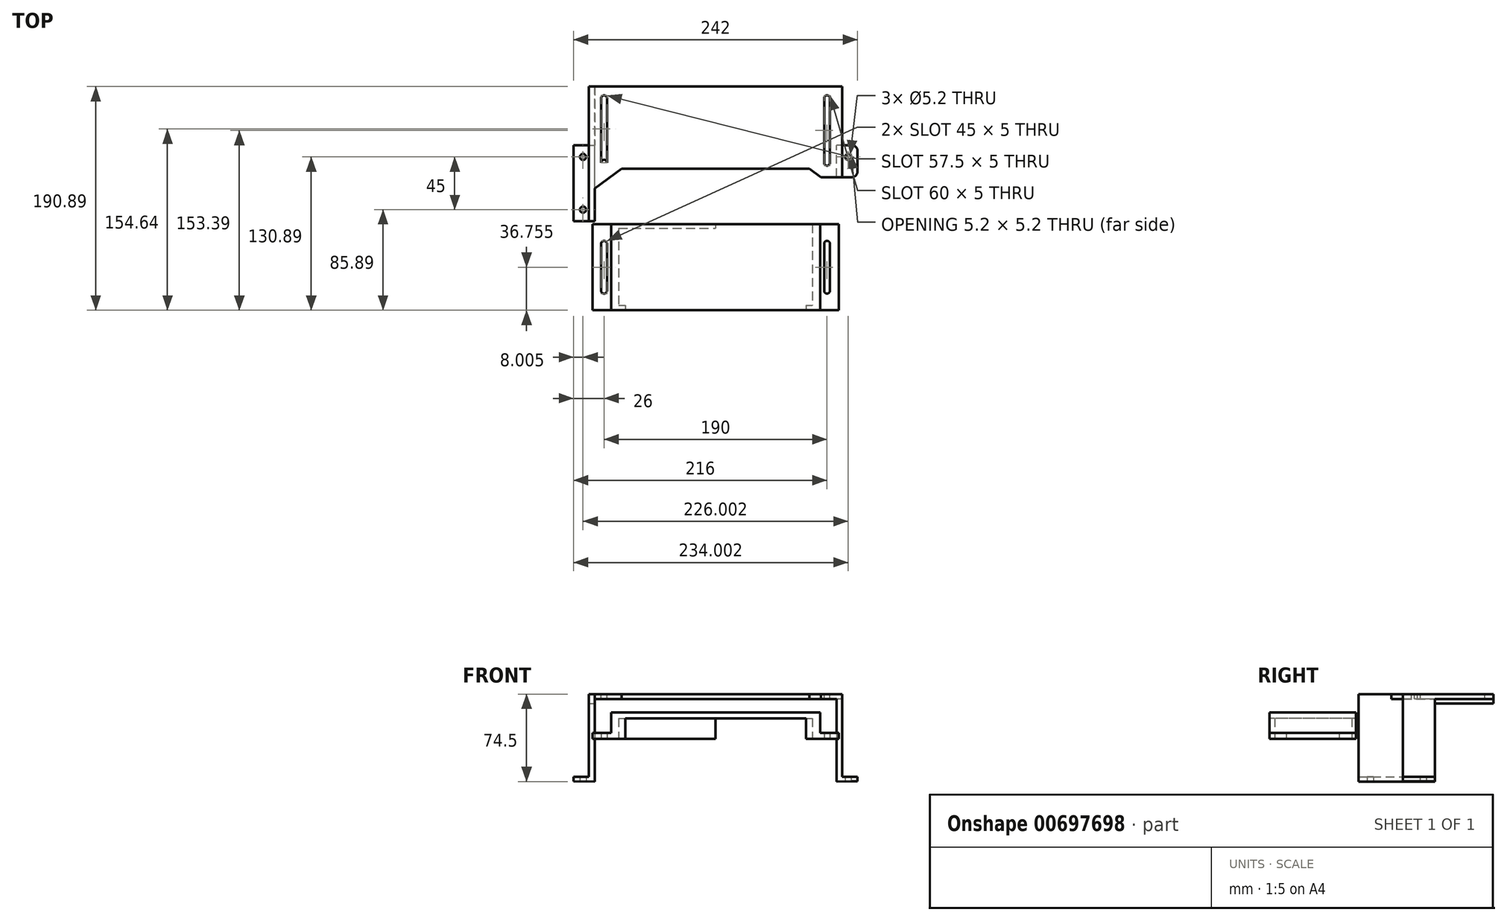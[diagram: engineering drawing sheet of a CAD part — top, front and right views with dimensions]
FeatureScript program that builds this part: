
annotation { "Feature Type Name" : "Feature", "Feature Type Description" : "" }
export const myFeature = defineFeature(function(context is Context, id is Id, definition is map)
    precondition{}
    {
        {
            var Q0;
            Q0=qCreatedBy(makeId("Front.planeOp"),FACE);
            var sketch = newSketch(context, id + "F0", { "sketchPlane" : qUnion([Q0])});
            skLineSegment(sketch, "E0.top", {"start": v(108, 38) * mm, "end": v(-108, 38) * mm});
            skPoint(sketch, "E0.middle", {"position": v(0, 0) * mm});
            skLineSegment(sketch, "E1.top", {"start": v(103, 34) * mm, "end": v(-103, 34) * mm});
            skLineSegment(sketch, "E2.MirrorCS", {"start": v(121, -32.45) * mm, "end": v(108, -32.5) * mm});
            skLineSegment(sketch, "E3.MirrorCS", {"start": v(121, -36.45) * mm, "end": v(121, -32.45) * mm});
            skLineSegment(sketch, "E4", {"start": v(108, 38) * mm, "end": v(108, -32.5) * mm});
            skLineSegment(sketch, "E5", {"start": v(121, -36.45) * mm, "end": v(103, -36.5) * mm});
            skLineSegment(sketch, "E6", {"start": v(103, 34) * mm, "end": v(103, -36.5) * mm});
            skLineSegment(sketch, "E7.MirrorCS", {"start": v(-103, 34) * mm, "end": v(-103, -36.5) * mm});
            skLineSegment(sketch, "E8.MirrorCS", {"start": v(-108, 38) * mm, "end": v(-108, -32.5) * mm});
            skLineSegment(sketch, "E9.MirrorCS", {"start": v(-121, -36.45) * mm, "end": v(-103, -36.5) * mm});
            skLineSegment(sketch, "E10.MirrorCS", {"start": v(-121, -36.45) * mm, "end": v(-121, -32.45) * mm});
            skLineSegment(sketch, "E11.MirrorCS", {"start": v(-121, -32.45) * mm, "end": v(-108, -32.5) * mm});
            skLineSegment(sketch, "E12", {"start": v(0, 34) * mm, "end": v(0, 0) * mm});
            skSolve(sketch);
        }
        {
            var Q0;
            Q0=makeQuery(id+"F0.imprint","IMPRINT",FACE,{"disambiguationData":[TD([[makeQuery(id+"F0.imprint","IMPRINT",EDGE,{"derivedFrom":sQuery(id+"F0.wireOp",EDGE,"E0.top")}),1.0]])]});
            extrude(context, id + "F1", {"entities" : qUnion([Q0]), "depth" : 65 * mm, "offsetDistance" : 25 * mm});
        }
        {
            var Q0;
            Q0=makeQuery(id+"F1.opExtrude","SWEPT_FACE",FACE,{"disambiguationData":[OSD([sQuery(id+"F0.wireOp",EDGE,"E0.top")])]});
            var sketch = newSketch(context, id + "F2", { "sketchPlane" : qUnion([Q0])});
            skLineSegment(sketch, "E13.bottom", {"start": v(80, -65) * mm, "end": v(-80, -65) * mm});
            skLineSegment(sketch, "E13.top", {"start": v(80, -20) * mm, "end": v(-80, -20) * mm});
            skLineSegment(sketch, "E13.left", {"start": v(80, -65) * mm, "end": v(80, -20) * mm});
            skLineSegment(sketch, "E13.right", {"start": v(-80, -65) * mm, "end": v(-80, -20) * mm});
            skPoint(sketch, "E13.middle", {"position": v(0, -42.5) * mm});
            skLineSegment(sketch, "E14.MirrorCS", {"start": v(80, -20) * mm, "end": v(107, -40) * mm});
            skLineSegment(sketch, "E15", {"start": v(107, -40) * mm, "end": v(107, -65) * mm});
            skLineSegment(sketch, "E16.MirrorCS", {"start": v(-80, -20) * mm, "end": v(-107, -40) * mm});
            skLineSegment(sketch, "E17.MirrorCS", {"start": v(-107, -40) * mm, "end": v(-107, -65) * mm});
            skLineSegment(sketch, "E18", {"start": v(108, -65) * mm, "end": v(112, -65) * mm});
            skLineSegment(sketch, "E19", {"start": v(112, -65) * mm, "end": v(112, 122.22) * mm});
            skLineSegment(sketch, "E20.MirrorCS", {"start": v(-112, -65) * mm, "end": v(-112, 122.22) * mm});
            skLineSegment(sketch, "E21", {"start": v(-103, -37.04) * mm, "end": v(-103, -65) * mm});
            skSolve(sketch);
        }
        {
            var Q0;
            Q0=makeQuery(id+"F2.imprint","IMPRINT",FACE,{"disambiguationData":[TD([[makeQuery(id+"F2.imprint","IMPRINT",EDGE,{"derivedFrom":sQuery(id+"F2.wireOp",EDGE,"E13.bottom")}),-1.0]])]});
            var Q1;
            {var subQ0=sQuery(id+"F2.wireOp",EDGE,"E13.left");Q1=makeQuery(id+"F2.imprint","IMPRINT",FACE,{"disambiguationData":[TD([[makeQuery(id+"F2.imprint","IMPRINT",EDGE,{"derivedFrom":subQ0}),-1.0]])]});}
            var Q2;
            {var subQ0=sQuery(id+"F2.wireOp",EDGE,"E13.right");Q2=makeQuery(id+"F2.imprint","IMPRINT",FACE,{"disambiguationData":[TD([[makeQuery(id+"F2.imprint","IMPRINT",EDGE,{"derivedFrom":subQ0}),1.0]])]});}
            var Q3;
            Q3=makeQuery(id+"F1.opExtrude","SWEPT_FACE",FACE,{"disambiguationData":[OSD([sQuery(id+"F0.wireOp",EDGE,"E1.top")])]});
            extrude(context, id + "F3", {"entities" : qUnion([Q0, Q1, Q2]), "operationType" : NewBodyOperationType.REMOVE, "endBound" : BoundingType.UP_TO_SURFACE, "oppositeDirection" : true, "depth" : 25 * mm, "endBoundEntityFace" : qUnion([Q3]), "offsetDistance" : 25 * mm});
        }
        {
            var Q0;
            Q0=makeQuery(id+"F1.opExtrude","CAP_FACE",FACE,{"disambiguationData":[OSD([sQuery(id+"F0.wireOp",EDGE,"E0.bottom"),sQuery(id+"F0.wireOp",EDGE,"E0.top"),sQuery(id+"F0.wireOp",EDGE,"E0.left"),sQuery(id+"F0.wireOp",EDGE,"E0.right"),sQuery(id+"F0.wireOp",EDGE,"E1.top"),sQuery(id+"F0.wireOp",EDGE,"E1.left"),sQuery(id+"F0.wireOp",EDGE,"E1.right"),sQuery(id+"F0.wireOp",EDGE,"vjw2G5nG-7NAh-i6nb-pNf6-F4kYSanWr40I.bottom"),sQuery(id+"F0.wireOp",EDGE,"vjw2G5nG-7NAh-i6nb-pNf6-F4kYSanWr40I.top"),sQuery(id+"F0.wireOp",EDGE,"vjw2G5nG-7NAh-i6nb-pNf6-F4kYSanWr40I.right"),sQuery(id+"F0.wireOp",EDGE,"50cf3a80-4362-4fa1-9d3c-48074abaa2c80.MirrorCS"),sQuery(id+"F0.wireOp",EDGE,"50cf3a80-4362-4fa1-9d3c-48074abaa2c81.MirrorCS"),sQuery(id+"F0.wireOp",EDGE,"50cf3a80-4362-4fa1-9d3c-48074abaa2c82.MirrorCS"),sQuery(id+"F0.wireOp",EDGE,"gSBNCoDe-7ixm-a6xe-L2ER-ax2OvEirnCgN"),sQuery(id+"F0.wireOp",EDGE,"e99ea971-1385-4194-99fd-02c7cae5d03b0.MirrorCS"),sQuery(id+"F0.wireOp",EDGE,"f15c71dd-c8da-4e97-9559-117df91addcc.trimOffspring")])],"isStart":true});
            var sketch = newSketch(context, id + "F4", { "sketchPlane" : qUnion([Q0])});
            skLineSegment(sketch, "E22.bottom", {"start": v(-108, 38) * mm, "end": v(103, 38) * mm});
            skLineSegment(sketch, "E22.top", {"start": v(-108, 34) * mm, "end": v(103, 34) * mm});
            skLineSegment(sketch, "E22.left", {"start": v(-108, 38) * mm, "end": v(-108, 34) * mm});
            skLineSegment(sketch, "E22.right", {"start": v(103, 38) * mm, "end": v(103, 34) * mm});
            skLineSegment(sketch, "E23.bottom", {"start": v(-108, 34) * mm, "end": v(-103, 34) * mm});
            skLineSegment(sketch, "E23.top", {"start": v(-108, 30) * mm, "end": v(-103, 30) * mm});
            skLineSegment(sketch, "E23.left", {"start": v(-108, 34) * mm, "end": v(-108, 30) * mm});
            skLineSegment(sketch, "E23.right", {"start": v(-103, 34) * mm, "end": v(-103, 30) * mm});
            skLineSegment(sketch, "E24.MirrorCS", {"start": v(108, 30) * mm, "end": v(103, 30) * mm});
            skLineSegment(sketch, "E25.MirrorCS", {"start": v(108, 34) * mm, "end": v(108, 30) * mm});
            skLineSegment(sketch, "E26.MirrorCS", {"start": v(103, 34) * mm, "end": v(103, 30) * mm});
            skSolve(sketch);
        }
        {
            var Q0;
            Q0=makeQuery(id+"F4.imprint","IMPRINT",FACE,{"disambiguationData":[TD([[makeQuery(id+"F4.imprint","IMPRINT",EDGE,{"derivedFrom":sQuery(id+"F4.wireOp",EDGE,"E22.bottom")}),-1.0]])]});
            var Q1;
            Q1=makeQuery(id+"F4.imprint","IMPRINT",FACE,{"disambiguationData":[TD([[makeQuery(id+"F4.imprint","IMPRINT",EDGE,{"derivedFrom":sQuery(id+"F4.wireOp",EDGE,"E23.bottom")}),-1.0]])]});
            var Q2;
            Q2=makeQuery(id+"F4.imprint","IMPRINT",FACE,{"disambiguationData":[TD([[makeQuery(id+"F4.imprint","IMPRINT",EDGE,{"derivedFrom":sQuery(id+"F4.wireOp",EDGE,"E24.MirrorCS")}),-1.0]])]});
            extrude(context, id + "F5", {"entities" : qUnion([Q0, Q1, Q2]), "operationType" : NewBodyOperationType.ADD, "depth" : 50 * mm, "offsetDistance" : 25 * mm});
        }
        {
            var Q0;
            Q0=makeQuery(id+"F5.boolean.opBoolean","MERGE",FACE,{"derivedFrom":[makeQuery(id+"F1.opExtrude","SWEPT_FACE",FACE,{"disambiguationData":[OSD([sQuery(id+"F0.wireOp",EDGE,"E0.left")])]}),makeQuery(id+"F5.opExtrude","SWEPT_FACE",FACE,{"disambiguationData":[OSD([sQuery(id+"F4.wireOp",EDGE,"E22.left"),sQuery(id+"F4.wireOp",EDGE,"E23.left")])]})]});
            var sketch = newSketch(context, id + "F6", { "sketchPlane" : qUnion([Q0])});
            skLineSegment(sketch, "E27.bottom", {"start": v(-27.27, 38) * mm, "end": v(-65, 38) * mm});
            skLineSegment(sketch, "E27.top", {"start": v(-27.27, -37.37) * mm, "end": v(-65, -37.37) * mm});
            skLineSegment(sketch, "E27.left", {"start": v(-27.27, 38) * mm, "end": v(-27.27, -37.37) * mm});
            skLineSegment(sketch, "E27.right", {"start": v(-65, 38) * mm, "end": v(-65, -37.37) * mm});
            skSolve(sketch);
        }
        {
            var Q0;
            {var subQ0=sQuery(id+"F6.wireOp",EDGE,"E27.bottom");Q0=makeQuery(id+"F6.imprint","IMPRINT",FACE,{"disambiguationData":[TD([[makeQuery(id+"F6.imprint","IMPRINT",EDGE,{"derivedFrom":subQ0}),-1.0]])]});}
            var Q1;
            {var subQ0=sQuery(id+"F6.wireOp",EDGE,"E27.top");Q1=makeQuery(id+"F6.imprint","IMPRINT",FACE,{"disambiguationData":[TD([[makeQuery(id+"F6.imprint","IMPRINT",EDGE,{"derivedFrom":subQ0}),-1.0]])]});}
            extrude(context, id + "F7", {"entities" : qUnion([Q0, Q1]), "operationType" : NewBodyOperationType.REMOVE, "oppositeDirection" : true, "depth" : 50 * mm, "offsetDistance" : 25 * mm, "symmetric" : true});
        }
        {
            var Q0;
            Q0=makeQuery(id+"F1.opExtrude","SWEPT_FACE",FACE,{"disambiguationData":[OSD([sQuery(id+"F0.wireOp",EDGE,"E9.MirrorCS")])]});
            var sketch = newSketch(context, id + "F8", { "sketchPlane" : qUnion([Q0])});
            skCircle(sketch, "E28", {"center": v(-112.9, 10) * mm, "radius": 2.6 * mm});
            skLineSegment(sketch, "E29", {"start": v(-112.9, 10) * mm, "end": v(-112.9, 55) * mm});
            skCircle(sketch, "E30", {"center": v(-112.9, 55) * mm, "radius": 2.6 * mm});
            skCircle(sketch, "E31.MirrorC", {"center": v(113.1, 55) * mm, "radius": 2.6 * mm});
            skCircle(sketch, "E32.MirrorC", {"center": v(113.1, 10) * mm, "radius": 2.6 * mm});
            skSolve(sketch);
        }
        {
            var Q0;
            Q0 = qSketchRegion(id + "F8", true);
            extrude(context, id + "F9", {"entities" : qUnion([Q0]), "operationType" : NewBodyOperationType.REMOVE, "oppositeDirection" : true, "depth" : 25 * mm, "offsetDistance" : 25 * mm});
        }
        {
            var Q0;
            Q0=makeQuery(id+"F1.opExtrude","CAP_EDGE",EDGE,{"disambiguationData":[OSD([sQuery(id+"F0.wireOp",EDGE,"vjw2G5nG-7NAh-i6nb-pNf6-F4kYSanWr40I.right")])],"isStart":false});
            var Q1;
            Q1=makeQuery(id+"F1.opExtrude","CAP_EDGE",EDGE,{"disambiguationData":[OSD([sQuery(id+"F0.wireOp",EDGE,"50cf3a80-4362-4fa1-9d3c-48074abaa2c80.MirrorCS"),sQuery(id+"F0.wireOp",EDGE,"E3.MirrorCS")])],"isStart":true});
            var Q2;
            Q2=makeQuery(id+"F7.boolean.opBoolean","INTERSECT",EDGE,{"derivedFrom":[makeQuery(id+"F1.opExtrude","SWEPT_FACE",FACE,{"disambiguationData":[OSD([sQuery(id+"F0.wireOp",EDGE,"50cf3a80-4362-4fa1-9d3c-48074abaa2c80.MirrorCS"),sQuery(id+"F0.wireOp",EDGE,"E3.MirrorCS")])]}),makeQuery(id+"F7.opExtrude","SWEPT_FACE",FACE,{"disambiguationData":[OSD([sQuery(id+"F6.wireOp",EDGE,"E27.left")])]})]});
            fillet(context, id + "F10", {"entities" : qUnion([Q0, Q1, Q2]), "radius" : 5 * mm, "tangentPropagation" : true, "allowEdgeOverflow" : false});
        }
        {
            var Q0;
            Q0=makeQuery(id+"F5.boolean.opBoolean","MERGE",FACE,{"derivedFrom":[makeQuery(id+"F1.opExtrude","SWEPT_FACE",FACE,{"disambiguationData":[OSD([sQuery(id+"F0.wireOp",EDGE,"E0.top")])]}),makeQuery(id+"F5.opExtrude","SWEPT_FACE",FACE,{"disambiguationData":[OSD([sQuery(id+"F4.wireOp",EDGE,"E22.bottom")])]})]});
            var sketch = newSketch(context, id + "F11", { "sketchPlane" : qUnion([Q0])});
            skLineSegment(sketch, "E33.bottom", {"start": v(-95, 0) * mm, "end": v(95, 0) * mm});
            skLineSegment(sketch, "E33.top", {"start": v(-95, 40) * mm, "end": v(95, 40) * mm});
            skLineSegment(sketch, "E33.left", {"start": v(-95, 0) * mm, "end": v(-95, 40) * mm});
            skLineSegment(sketch, "E33.right", {"start": v(95, 0) * mm, "end": v(95, 40) * mm});
            skPoint(sketch, "E33.middle", {"position": v(0, 20) * mm});
            skCircle(sketch, "E34", {"center": v(-95, 40) * mm, "radius": 2.5 * mm});
            skLineSegment(sketch, "E35.bottom", {"start": v(82.5, -12.75) * mm, "end": v(-82.5, -12.75) * mm});
            skLineSegment(sketch, "E35.top", {"start": v(82.5, 52.75) * mm, "end": v(-82.5, 52.75) * mm});
            skLineSegment(sketch, "E35.left", {"start": v(82.5, -12.75) * mm, "end": v(82.5, 52.75) * mm});
            skLineSegment(sketch, "E35.right", {"start": v(-82.5, -12.75) * mm, "end": v(-82.5, 52.75) * mm});
            skLineSegment(sketch, "E36", {"start": v(0, 20) * mm, "end": v(12, 20) * mm});
            skCircle(sketch, "E37.MirrorC", {"center": v(-95, 0) * mm, "radius": 2.5 * mm});
            skCircle(sketch, "E38.MirrorC", {"center": v(95, 40) * mm, "radius": 2.5 * mm});
            skCircle(sketch, "E39.MirrorC", {"center": v(95, 0) * mm, "radius": 2.5 * mm});
            skLineSegment(sketch, "E40", {"start": v(95, 0) * mm, "end": v(95, -15) * mm});
            skCircle(sketch, "E41", {"center": v(95, -15) * mm, "radius": 2.5 * mm});
            skLineSegment(sketch, "E42", {"start": v(97.5, -15) * mm, "end": v(97.5, 40) * mm});
            skLineSegment(sketch, "E43", {"start": v(92.5, -15) * mm, "end": v(92.5, 40) * mm});
            skLineSegment(sketch, "E44.MirrorCS", {"start": v(-92.5, -15) * mm, "end": v(-92.5, 40) * mm});
            skLineSegment(sketch, "E45.MirrorCS", {"start": v(-97.5, -15) * mm, "end": v(-97.5, 40) * mm});
            skCircle(sketch, "E46.MirrorC", {"center": v(-95, -15) * mm, "radius": 2.5 * mm});
            skSolve(sketch);
        }
        {
            var Q0;
            {var subQ0=sQuery(id+"F11.wireOp",EDGE,"E33.left");var subQ1=sQuery(id+"F11.wireOp",EDGE,"E33.top");var subQ2=makeQuery(id+"F11.imprint","INTERSECT",VERTEX,{"derivedFrom":[subQ1,subQ0]});Q0=makeQuery(id+"F11.imprint","IMPRINT",FACE,{"disambiguationData":[TD([[makeQuery(id+"F11.imprint","IMPRINT",EDGE,{"disambiguationData":[TD([[subQ2,-1.0]])],"derivedFrom":subQ1}),1.0]])]});}
            var Q1;
            {var subQ0=sQuery(id+"F11.wireOp",EDGE,"E33.left");var subQ1=sQuery(id+"F11.wireOp",EDGE,"E33.top");var subQ2=makeQuery(id+"F11.imprint","INTERSECT",VERTEX,{"derivedFrom":[subQ1,subQ0]});Q1=makeQuery(id+"F11.imprint","IMPRINT",FACE,{"disambiguationData":[TD([[makeQuery(id+"F11.imprint","IMPRINT",EDGE,{"disambiguationData":[TD([[subQ2,-1.0]])],"derivedFrom":subQ1}),-1.0]])]});}
            var Q2;
            {var subQ0=sQuery(id+"F11.wireOp",EDGE,"E33.left");var subQ1=sQuery(id+"F11.wireOp",EDGE,"E33.bottom");var subQ2=makeQuery(id+"F11.imprint","INTERSECT",VERTEX,{"derivedFrom":[subQ1,subQ0]});Q2=makeQuery(id+"F11.imprint","IMPRINT",FACE,{"disambiguationData":[TD([[makeQuery(id+"F11.imprint","IMPRINT",EDGE,{"disambiguationData":[TD([[subQ2,-1.0]])],"derivedFrom":subQ1}),-1.0]])]});}
            var Q3;
            {var subQ0=sQuery(id+"F11.wireOp",EDGE,"E33.left");var subQ1=sQuery(id+"F11.wireOp",EDGE,"E33.bottom");var subQ2=makeQuery(id+"F11.imprint","INTERSECT",VERTEX,{"derivedFrom":[subQ1,subQ0]});Q3=makeQuery(id+"F11.imprint","IMPRINT",FACE,{"disambiguationData":[TD([[makeQuery(id+"F11.imprint","IMPRINT",EDGE,{"disambiguationData":[TD([[subQ2,-1.0]])],"derivedFrom":subQ1}),1.0]])]});}
            var Q4;
            {var subQ0=sQuery(id+"F11.wireOp",EDGE,"E33.right");var subQ1=sQuery(id+"F11.wireOp",EDGE,"E33.bottom");var subQ2=makeQuery(id+"F11.imprint","INTERSECT",VERTEX,{"derivedFrom":[subQ1,subQ0]});Q4=makeQuery(id+"F11.imprint","IMPRINT",FACE,{"disambiguationData":[TD([[makeQuery(id+"F11.imprint","IMPRINT",EDGE,{"disambiguationData":[TD([[subQ2,1.0]])],"derivedFrom":subQ1}),-1.0]])]});}
            var Q5;
            {var subQ0=sQuery(id+"F11.wireOp",EDGE,"E33.right");var subQ1=sQuery(id+"F11.wireOp",EDGE,"E33.bottom");var subQ2=makeQuery(id+"F11.imprint","INTERSECT",VERTEX,{"derivedFrom":[subQ1,subQ0]});Q5=makeQuery(id+"F11.imprint","IMPRINT",FACE,{"disambiguationData":[TD([[makeQuery(id+"F11.imprint","IMPRINT",EDGE,{"disambiguationData":[TD([[subQ2,1.0]])],"derivedFrom":subQ1}),1.0]])]});}
            var Q6;
            {var subQ0=sQuery(id+"F11.wireOp",EDGE,"E33.right");var subQ1=sQuery(id+"F11.wireOp",EDGE,"E33.top");var subQ2=makeQuery(id+"F11.imprint","INTERSECT",VERTEX,{"derivedFrom":[subQ1,subQ0]});Q6=makeQuery(id+"F11.imprint","IMPRINT",FACE,{"disambiguationData":[TD([[makeQuery(id+"F11.imprint","IMPRINT",EDGE,{"disambiguationData":[TD([[subQ2,1.0]])],"derivedFrom":subQ1}),1.0]])]});}
            var Q7;
            {var subQ0=sQuery(id+"F11.wireOp",EDGE,"E33.right");var subQ1=sQuery(id+"F11.wireOp",EDGE,"E33.top");var subQ2=makeQuery(id+"F11.imprint","INTERSECT",VERTEX,{"derivedFrom":[subQ1,subQ0]});Q7=makeQuery(id+"F11.imprint","IMPRINT",FACE,{"disambiguationData":[TD([[makeQuery(id+"F11.imprint","IMPRINT",EDGE,{"disambiguationData":[TD([[subQ2,1.0]])],"derivedFrom":subQ1}),-1.0]])]});}
            var Q8;
            {var subQ0=sQuery(id+"F11.wireOp",EDGE,"E39.MirrorC");var subQ1=sQuery(id+"F11.wireOp",EDGE,"E33.right");var subQ2=makeQuery(id+"F11.imprint","INTERSECT",VERTEX,{"derivedFrom":[subQ1,subQ0]});Q8=makeQuery(id+"F11.imprint","IMPRINT",FACE,{"disambiguationData":[TD([[makeQuery(id+"F11.imprint","IMPRINT",EDGE,{"disambiguationData":[TD([[subQ2,-1.0]])],"derivedFrom":subQ1}),-1.0]])]});}
            var Q9;
            {var subQ0=sQuery(id+"F11.wireOp",EDGE,"E40");var subQ3=sQuery(id+"F11.wireOp",EDGE,"E39.MirrorC");var subQ5=makeQuery(id+"F11.imprint","INTERSECT",VERTEX,{"derivedFrom":[subQ3,subQ0]});Q9=makeQuery(id+"F11.imprint","IMPRINT",FACE,{"disambiguationData":[TD([[makeQuery(id+"F11.imprint","IMPRINT",EDGE,{"disambiguationData":[TD([[subQ5,-1.0]])],"derivedFrom":subQ3}),1.0]])]});}
            var Q10;
            {var subQ0=sQuery(id+"F11.wireOp",EDGE,"E40");var subQ1=sQuery(id+"F11.wireOp",EDGE,"E39.MirrorC");var subQ2=makeQuery(id+"F11.imprint","INTERSECT",VERTEX,{"derivedFrom":[subQ1,subQ0]});Q10=makeQuery(id+"F11.imprint","IMPRINT",FACE,{"disambiguationData":[TD([[makeQuery(id+"F11.imprint","IMPRINT",EDGE,{"disambiguationData":[TD([[subQ2,-1.0]])],"derivedFrom":subQ1}),-1.0]])]});}
            var Q11;
            {var subQ0=sQuery(id+"F11.wireOp",EDGE,"E41");var subQ1=makeQuery(id+"F11.imprint","INTERSECT",VERTEX,{"derivedFrom":[subQ0,sQuery(id+"F11.wireOp",EDGE,"E42")]});Q11=makeQuery(id+"F11.imprint","IMPRINT",FACE,{"disambiguationData":[TD([[makeQuery(id+"F11.imprint","IMPRINT",EDGE,{"disambiguationData":[TD([[subQ1,-1.0]])],"derivedFrom":subQ0}),1.0]])]});}
            var Q12;
            {var subQ0=sQuery(id+"F11.wireOp",EDGE,"E39.MirrorC");var subQ1=sQuery(id+"F11.wireOp",EDGE,"E33.right");var subQ2=makeQuery(id+"F11.imprint","INTERSECT",VERTEX,{"derivedFrom":[subQ1,subQ0]});Q12=makeQuery(id+"F11.imprint","IMPRINT",FACE,{"disambiguationData":[TD([[makeQuery(id+"F11.imprint","IMPRINT",EDGE,{"disambiguationData":[TD([[subQ2,-1.0]])],"derivedFrom":subQ1}),1.0]])]});}
            var Q13;
            {var subQ0=sQuery(id+"F11.wireOp",EDGE,"E40");var subQ5=sQuery(id+"F11.wireOp",EDGE,"E41");var subQ6=makeQuery(id+"F11.imprint","INTERSECT",VERTEX,{"derivedFrom":[subQ0,subQ5]});Q13=makeQuery(id+"F11.imprint","IMPRINT",FACE,{"disambiguationData":[TD([[makeQuery(id+"F11.imprint","IMPRINT",EDGE,{"disambiguationData":[TD([[subQ6,1.0]])],"derivedFrom":subQ0}),-1.0]])]});}
            var Q14;
            {var subQ0=sQuery(id+"F11.wireOp",EDGE,"E37.MirrorC");var subQ1=sQuery(id+"F11.wireOp",EDGE,"E33.left");var subQ2=makeQuery(id+"F11.imprint","INTERSECT",VERTEX,{"derivedFrom":[subQ1,subQ0]});Q14=makeQuery(id+"F11.imprint","IMPRINT",FACE,{"disambiguationData":[TD([[makeQuery(id+"F11.imprint","IMPRINT",EDGE,{"disambiguationData":[TD([[subQ2,-1.0]])],"derivedFrom":subQ1}),-1.0]])]});}
            var Q15;
            {var subQ0=sQuery(id+"F11.wireOp",EDGE,"E37.MirrorC");var subQ1=sQuery(id+"F11.wireOp",EDGE,"E33.left");var subQ2=makeQuery(id+"F11.imprint","INTERSECT",VERTEX,{"derivedFrom":[subQ1,subQ0]});Q15=makeQuery(id+"F11.imprint","IMPRINT",FACE,{"disambiguationData":[TD([[makeQuery(id+"F11.imprint","IMPRINT",EDGE,{"disambiguationData":[TD([[subQ2,-1.0]])],"derivedFrom":subQ1}),1.0]])]});}
            var Q16;
            {var subQ0=sQuery(id+"F11.wireOp",EDGE,"E46.MirrorC");var subQ1=makeQuery(id+"F11.imprint","INTERSECT",VERTEX,{"derivedFrom":[sQuery(id+"F11.wireOp",EDGE,"E44.MirrorCS"),subQ0]});Q16=makeQuery(id+"F11.imprint","IMPRINT",FACE,{"disambiguationData":[TD([[makeQuery(id+"F11.imprint","IMPRINT",EDGE,{"disambiguationData":[TD([[subQ1,1.0]])],"derivedFrom":subQ0}),-1.0]])]});}
            var Q17;
            {var subQ0=sQuery(id+"F11.wireOp",EDGE,"E45.MirrorCS");var subQ5=sQuery(id+"F11.wireOp",EDGE,"E46.MirrorC");var subQ7=makeQuery(id+"F11.imprint","INTERSECT",VERTEX,{"derivedFrom":[subQ0,subQ5]});Q17=makeQuery(id+"F11.imprint","IMPRINT",FACE,{"disambiguationData":[TD([[makeQuery(id+"F11.imprint","IMPRINT",EDGE,{"disambiguationData":[TD([[subQ7,-1.0]])],"derivedFrom":subQ0}),-1.0]])]});}
            extrude(context, id + "F12", {"entities" : qUnion([Q0, Q1, Q2, Q3, Q4, Q5, Q6, Q7, Q8, Q9, Q10, Q11, Q12, Q13, Q14, Q15, Q16, Q17]), "operationType" : NewBodyOperationType.REMOVE, "oppositeDirection" : true, "depth" : 25 * mm, "offsetDistance" : 25 * mm});
        }
        {
            var Q0;
            Q0=qCreatedBy(makeId("Top.planeOp"),FACE);
            var sketch = newSketch(context, id + "F13", { "sketchPlane" : qUnion([Q0])});
            skLineSegment(sketch, "E47.bottom", {"start": v(105, -140.89) * mm, "end": v(-105, -140.89) * mm});
            skLineSegment(sketch, "E47.top", {"start": v(105, -67.39) * mm, "end": v(-105, -67.39) * mm});
            skLineSegment(sketch, "E47.left", {"start": v(105, -140.89) * mm, "end": v(105, -67.39) * mm});
            skLineSegment(sketch, "E47.right", {"start": v(-105, -140.89) * mm, "end": v(-105, -67.39) * mm});
            skPoint(sketch, "E47.middle", {"position": v(0, -104.14) * mm});
            skLineSegment(sketch, "E48.bottom", {"start": v(95, -124.14) * mm, "end": v(-95, -124.14) * mm});
            skLineSegment(sketch, "E48.top", {"start": v(95, -84.14) * mm, "end": v(-95, -84.14) * mm});
            skLineSegment(sketch, "E48.left", {"start": v(95, -124.14) * mm, "end": v(95, -84.14) * mm});
            skLineSegment(sketch, "E48.right", {"start": v(-95, -124.14) * mm, "end": v(-95, -84.14) * mm});
            skCircle(sketch, "E49", {"center": v(-95, -84.14) * mm, "radius": 2.5 * mm});
            skLineSegment(sketch, "E50", {"start": v(0, -104.14) * mm, "end": v(0, -114.51) * mm});
            skLineSegment(sketch, "E51", {"start": v(0, -114.51) * mm, "end": v(0, -104.14) * mm});
            skLineSegment(sketch, "E52", {"start": v(11.3, -104.14) * mm, "end": v(0, -104.14) * mm});
            skCircle(sketch, "E53.MirrorC", {"center": v(-95, -124.14) * mm, "radius": 2.5 * mm});
            skCircle(sketch, "E54.MirrorC", {"center": v(95, -84.14) * mm, "radius": 2.5 * mm});
            skCircle(sketch, "E55.MirrorC", {"center": v(95, -124.14) * mm, "radius": 2.5 * mm});
            skLineSegment(sketch, "E56", {"start": v(97.5, -124.14) * mm, "end": v(97.5, -84.14) * mm});
            skLineSegment(sketch, "E57.MirrorCS", {"start": v(92.5, -124.14) * mm, "end": v(92.5, -84.14) * mm});
            skLineSegment(sketch, "E58.MirrorCS", {"start": v(-92.5, -124.14) * mm, "end": v(-92.5, -84.14) * mm});
            skLineSegment(sketch, "E59.MirrorCS", {"start": v(-97.5, -124.14) * mm, "end": v(-97.5, -84.14) * mm});
            skSolve(sketch);
        }
        {
            var Q0;
            Q0 = qSketchRegion(id + "F13", true);
            var Q1;
            {var subQ5=sQuery(id+"F13.wireOp",EDGE,"E55.MirrorC");var subQ13=sQuery(id+"F13.wireOp",EDGE,"E48.bottom");var subQ15=makeQuery(id+"F13.imprint","INTERSECT",VERTEX,{"derivedFrom":[subQ13,subQ5]});Q1=makeQuery(id+"F13.imprint","IMPRINT",FACE,{"disambiguationData":[TD([[makeQuery(id+"F13.imprint","IMPRINT",EDGE,{"disambiguationData":[TD([[subQ15,-1.0]])],"derivedFrom":subQ13}),-1.0]])]});}
            extrude(context, id + "F14", {"entities" : qUnion([Q0, Q1]), "depth" : 5 * mm, "offsetDistance" : 25 * mm});
        }
        {
            var Q0;
            Q0=makeQuery(id+"F14.opExtrude","CAP_FACE",FACE,{"disambiguationData":[OSD([sQuery(id+"F13.wireOp",EDGE,"E47.bottom"),sQuery(id+"F13.wireOp",EDGE,"E47.top"),sQuery(id+"F13.wireOp",EDGE,"E47.left"),sQuery(id+"F13.wireOp",EDGE,"E47.right"),sQuery(id+"F13.wireOp",EDGE,"E49"),sQuery(id+"F13.wireOp",EDGE,"E53.MirrorC"),sQuery(id+"F13.wireOp",EDGE,"E54.MirrorC"),sQuery(id+"F13.wireOp",EDGE,"E55.MirrorC")])],"isStart":false});
            var sketch = newSketch(context, id + "F15", { "sketchPlane" : qUnion([Q0])});
            skLineSegment(sketch, "E60.bottom", {"start": v(89, -140.89) * mm, "end": v(-89, -140.89) * mm});
            skLineSegment(sketch, "E60.top", {"start": v(89, -67.39) * mm, "end": v(-89, -67.39) * mm});
            skLineSegment(sketch, "E60.left", {"start": v(89, -140.89) * mm, "end": v(89, -67.39) * mm});
            skLineSegment(sketch, "E60.right", {"start": v(-89, -140.89) * mm, "end": v(-89, -67.39) * mm});
            skPoint(sketch, "E60.middle", {"position": v(0, -104.14) * mm});
            skPoint(sketch, "E60.middle.positionSnap0", {"position": v(0, -67.39) * mm});
            skPoint(sketch, "E60.centerSnap0", {"position": v(0, -67.39) * mm});
            skSolve(sketch);
        }
        {
            var Q0;
            Q0 = qSketchRegion(id + "F15", true);
            extrude(context, id + "F16", {"entities" : qUnion([Q0]), "operationType" : NewBodyOperationType.ADD, "depth" : 17.5 * mm, "offsetDistance" : 25 * mm});
        }
        {
            var Q0;
            Q0=makeQuery(id+"F14.opExtrude","CAP_FACE",FACE,{"disambiguationData":[OSD([sQuery(id+"F13.wireOp",EDGE,"E47.bottom"),sQuery(id+"F13.wireOp",EDGE,"E47.top"),sQuery(id+"F13.wireOp",EDGE,"E47.left"),sQuery(id+"F13.wireOp",EDGE,"E47.right"),sQuery(id+"F13.wireOp",EDGE,"E49"),sQuery(id+"F13.wireOp",EDGE,"E53.MirrorC"),sQuery(id+"F13.wireOp",EDGE,"E54.MirrorC"),sQuery(id+"F13.wireOp",EDGE,"E55.MirrorC")])],"isStart":true});
            var sketch = newSketch(context, id + "F17", { "sketchPlane" : qUnion([Q0])});
            skLineSegment(sketch, "E61.bottom", {"start": v(-82.6, 70.8) * mm, "end": v(82.6, 70.8) * mm});
            skLineSegment(sketch, "E61.top", {"start": v(-82.6, 136.5) * mm, "end": v(82.6, 136.5) * mm});
            skLineSegment(sketch, "E61.left", {"start": v(-82.6, 70.8) * mm, "end": v(-82.6, 136.5) * mm});
            skLineSegment(sketch, "E61.right", {"start": v(82.6, 70.8) * mm, "end": v(82.6, 136.5) * mm});
            skPoint(sketch, "E61.middle", {"position": v(0, 103.64) * mm});
            skSolve(sketch);
        }
        {
            var Q0;
            Q0=makeQuery(id+"F17.imprint","IMPRINT",FACE,{"disambiguationData":[TD([[makeQuery(id+"F17.imprint","IMPRINT",EDGE,{"derivedFrom":sQuery(id+"F17.wireOp",EDGE,"E61.bottom")}),1.0]])]});
            extrude(context, id + "F18", {"entities" : qUnion([Q0]), "operationType" : NewBodyOperationType.REMOVE, "oppositeDirection" : true, "depth" : 17.5 * mm, "offsetDistance" : 25 * mm});
        }
        {
            var Q0;
            Q0=makeQuery(id+"F16.boolean.opBoolean","MERGE",FACE,{"derivedFrom":[makeQuery(id+"F14.opExtrude","SWEPT_FACE",FACE,{"disambiguationData":[OSD([sQuery(id+"F13.wireOp",EDGE,"E47.bottom")])]}),makeQuery(id+"F16.opExtrude","SWEPT_FACE",FACE,{"disambiguationData":[OSD([sQuery(id+"F15.wireOp",EDGE,"E60.bottom")])]})]});
            var sketch = newSketch(context, id + "F19", { "sketchPlane" : qUnion([Q0])});
            skLineSegment(sketch, "E62.bottom", {"start": v(-77, 0) * mm, "end": v(77, 0) * mm});
            skLineSegment(sketch, "E62.top", {"start": v(-77, 17.5) * mm, "end": v(77, 17.5) * mm});
            skLineSegment(sketch, "E62.left", {"start": v(-77, 0) * mm, "end": v(-77, 17.5) * mm});
            skLineSegment(sketch, "E62.right", {"start": v(77, 0) * mm, "end": v(77, 17.5) * mm});
            skSolve(sketch);
        }
        {
            var Q0;
            Q0=makeQuery(id+"F19.imprint","IMPRINT",FACE,{"disambiguationData":[TD([[makeQuery(id+"F19.imprint","IMPRINT",EDGE,{"derivedFrom":sQuery(id+"F19.wireOp",EDGE,"E62.bottom")}),-1.0]])]});
            extrude(context, id + "F20", {"entities" : qUnion([Q0]), "operationType" : NewBodyOperationType.REMOVE, "oppositeDirection" : true, "depth" : 25 * mm, "offsetDistance" : 25 * mm});
        }
        {
            var Q0;
            Q0=makeQuery(id+"F18.boolean.opBoolean","COPY",FACE,{"derivedFrom":makeQuery(id+"F18.opExtrude","SWEPT_FACE",FACE,{"disambiguationData":[OSD([sQuery(id+"F17.wireOp",EDGE,"E61.bottom")])]})});
            var sketch = newSketch(context, id + "F21", { "sketchPlane" : qUnion([Q0])});
            skLineSegment(sketch, "E63.bottom", {"start": v(82.6, 17.5) * mm, "end": v(0, 17.5) * mm});
            skLineSegment(sketch, "E63.top", {"start": v(82.6, 0) * mm, "end": v(0, 0) * mm});
            skLineSegment(sketch, "E63.left", {"start": v(82.6, 17.5) * mm, "end": v(82.6, 0) * mm});
            skLineSegment(sketch, "E63.right", {"start": v(0, 17.5) * mm, "end": v(0, 0) * mm});
            skSolve(sketch);
        }
        {
            var Q0;
            Q0 = qSketchRegion(id + "F21", true);
            extrude(context, id + "F22", {"entities" : qUnion([Q0]), "operationType" : NewBodyOperationType.REMOVE, "oppositeDirection" : true, "depth" : 25 * mm, "offsetDistance" : 25 * mm});
        }
    });
